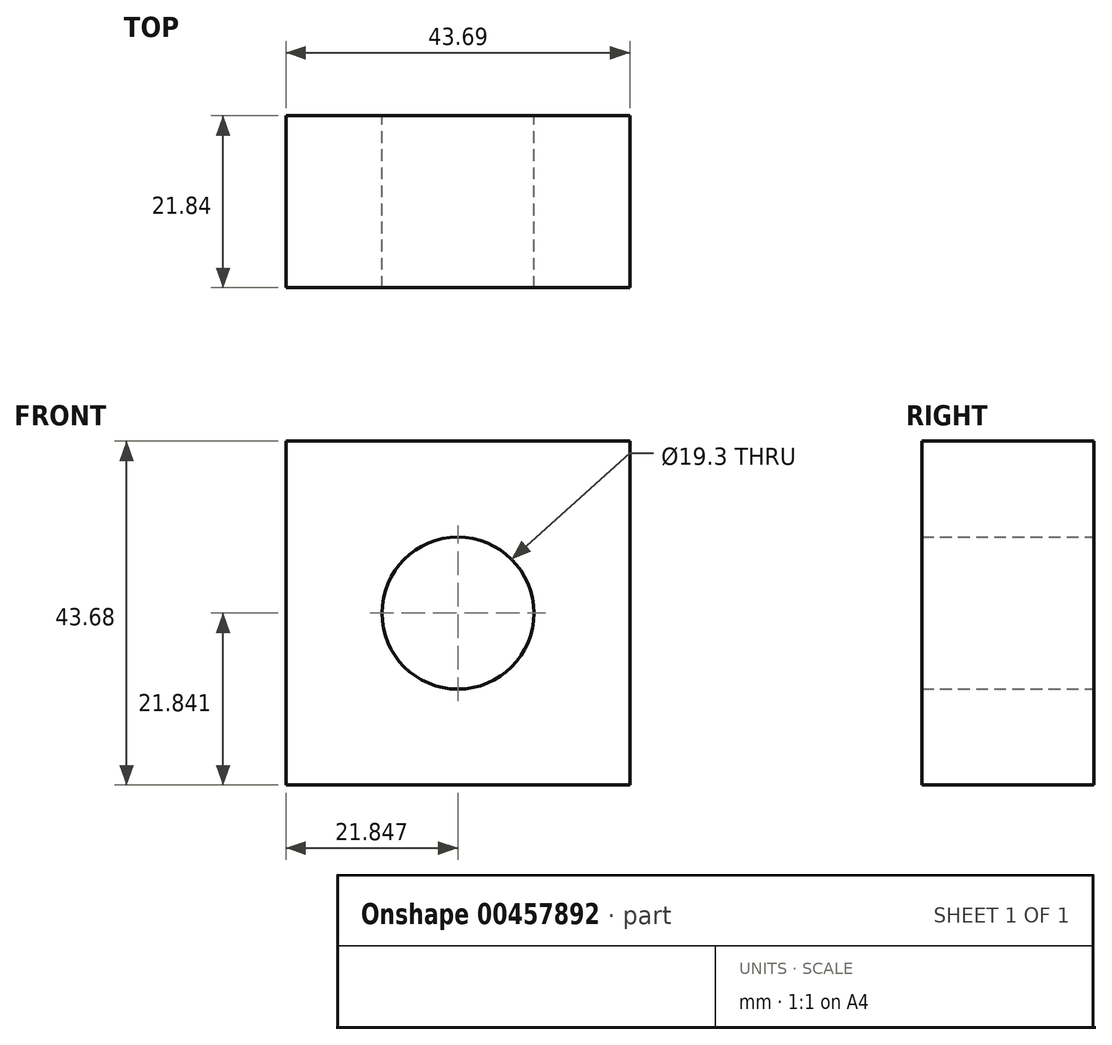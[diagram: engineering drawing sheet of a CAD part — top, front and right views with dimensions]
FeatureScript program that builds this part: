
annotation { "Feature Type Name" : "Feature", "Feature Type Description" : "" }
export const myFeature = defineFeature(function(context is Context, id is Id, definition is map)
    precondition{}
    {
        {
            var Q0;
            Q0=qCreatedBy(makeId("Front.planeOp"),FACE);
            var sketch = newSketch(context, id + "F0", { "sketchPlane" : qUnion([Q0])});
            skLineSegment(sketch, "E0", {"start": v(-59.44, 33.7) * mm, "end": v(-59.44, -9.98) * mm});
            skLineSegment(sketch, "E1", {"start": v(-59.44, -9.98) * mm, "end": v(-15.75, -9.98) * mm});
            skLineSegment(sketch, "E2", {"start": v(-15.75, -9.98) * mm, "end": v(-15.75, 33.7) * mm});
            skLineSegment(sketch, "E3", {"start": v(-15.75, 33.7) * mm, "end": v(-59.44, 33.7) * mm});
            skCircle(sketch, "E4", {"center": v(-37.6, 11.86) * mm, "radius": 9.65 * mm});
            skSolve(sketch);
        }
        {
            var Q0;
            Q0 = qSketchRegion(id + "F0", true);
            extrude(context, id + "F1", {"entities" : qUnion([Q0]), "depth" : 21.84 * mm});
        }
    });
